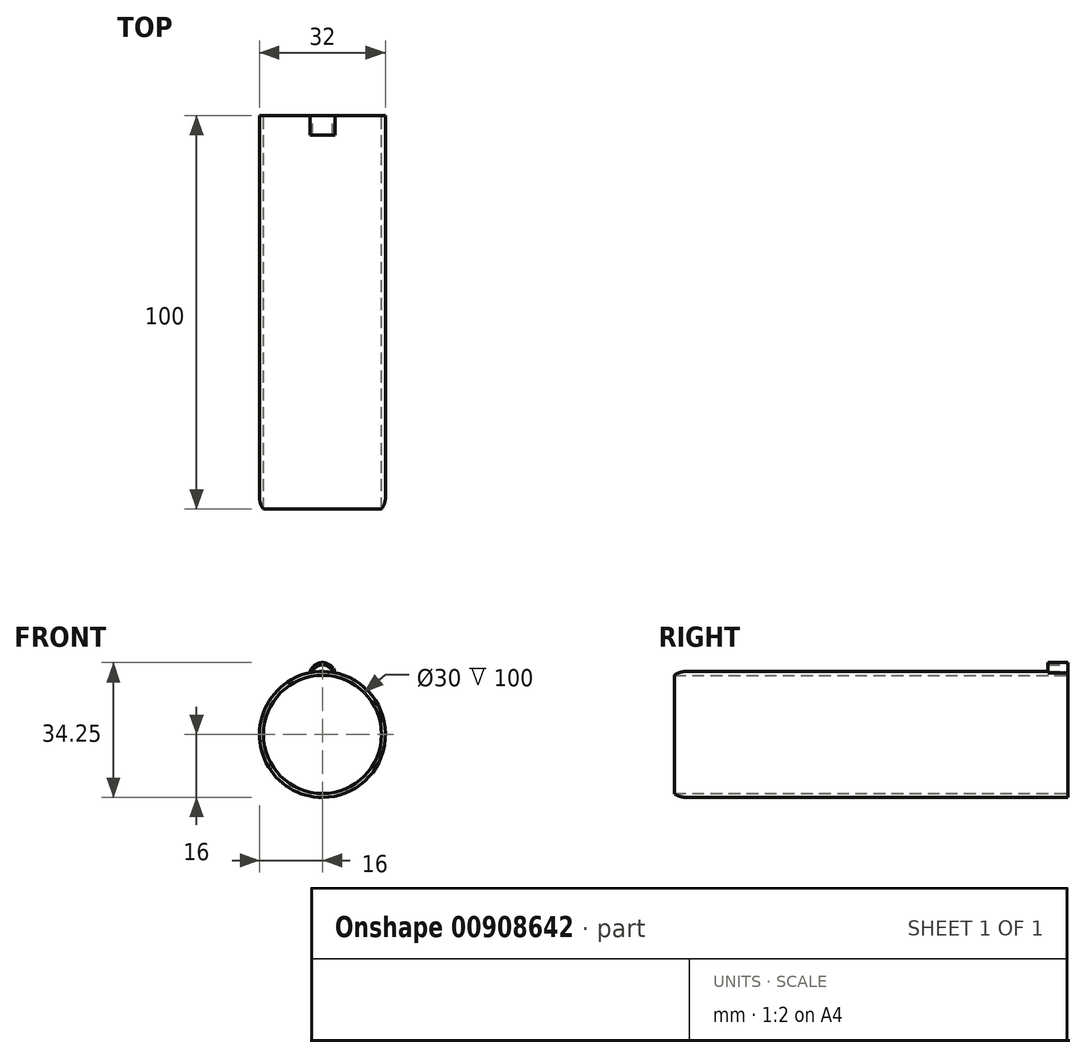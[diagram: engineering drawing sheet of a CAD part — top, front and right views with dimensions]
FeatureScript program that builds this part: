
annotation { "Feature Type Name" : "Feature", "Feature Type Description" : "" }
export const myFeature = defineFeature(function(context is Context, id is Id, definition is map)
    precondition{}
    {
        {
            var Q0;
            Q0=qCreatedBy(makeId("Front.planeOp"),FACE);
            var sketch = newSketch(context, id + "F0", { "sketchPlane" : qUnion([Q0])});
            skCircle(sketch, "E0", {"center": v(0, 0) * mm, "radius": 15 * mm});
            skArc(sketch, "E1", {"start": v(2.58, 15.8) * mm, "mid": v(0, 17.7) * mm, "end": v(-2.58, 15.8) * mm});
            skArc(sketch, "E2", {"start": v(3.18, 15.68) * mm, "mid": v(0, 18.25) * mm, "end": v(-3.18, 15.68) * mm});
            skCircle(sketch, "E3", {"center": v(0, 0) * mm, "radius": 16 * mm});
            skSolve(sketch);
        }
        {
            var Q0;
            Q0=makeQuery(id+"F0.imprint","IMPRINT",FACE,{"disambiguationData":[TD([[makeQuery(id+"F0.imprint","IMPRINT",EDGE,{"derivedFrom":sQuery(id+"F0.wireOp",EDGE,"E0")}),-1.0]])]});
            extrude(context, id + "F1", {"entities" : qUnion([Q0]), "depth" : 100 * mm, "offsetDistance" : 25 * mm});
        }
        {
            var Q0;
            Q0 = qSketchRegion(id + "F0", true);
            extrude(context, id + "F2", {"entities" : qUnion([Q0]), "operationType" : NewBodyOperationType.ADD, "depth" : 5 * mm, "offsetDistance" : 25 * mm});
        }
        {
            var Q0;
            Q0=makeQuery(id+"F1.opExtrude","CAP_EDGE",EDGE,{"disambiguationData":[OSD([sQuery(id+"F0.wireOp",EDGE,"E3")])],"isStart":false});
            fillet(context, id + "F3", {"entities" : qUnion([Q0]), "radius" : 5 * mm, "tangentPropagation" : true, "allowEdgeOverflow" : false});
        }
    });
